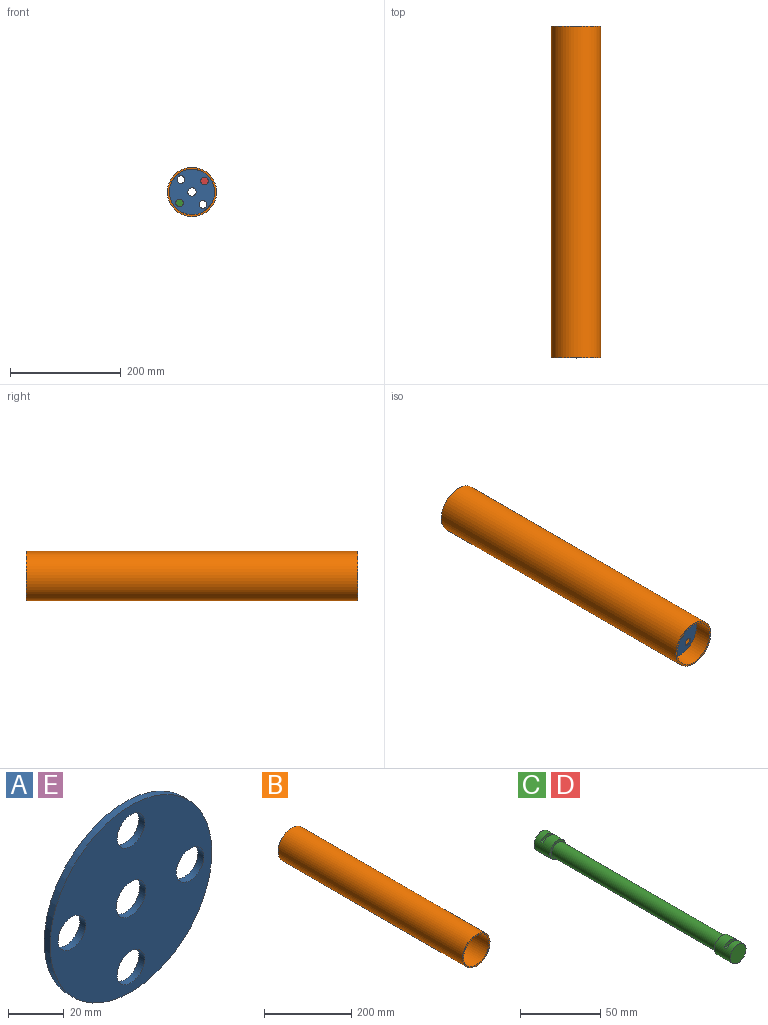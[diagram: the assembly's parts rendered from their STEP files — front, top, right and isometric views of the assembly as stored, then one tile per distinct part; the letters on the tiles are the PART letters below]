
ASSEMBLY  parts=5 mates=8
PART A: 8 faces, bbox 82x3x82 mm
  f0: cylinder r=7mm len=14mm, axis (0,1,0), area 131.9mm2, adj f5,f6
  f1: cylinder r=7mm len=14mm, axis (0,1,0), area 131.9mm2, adj f5,f6
  f2: cylinder r=7mm len=14mm, axis (0,1,0), area 131.9mm2, adj f5,f6
  f3: cylinder r=7mm len=14mm, axis (0,1,0), area 131.9mm2, adj f5,f6
  f4: cylinder r=41mm len=82mm, axis (0,1,0), area 772.8mm2, adj f5,f6
  f5: plane 82x82mm, normal (0,-1,0), area 4488.6mm2, adj f0,f1,f2,f3,f4,f7
  f6: plane 82x82mm, normal (0,1,0), area 4488.6mm2, adj f0,f1,f2,f3,f4,f7
  f7: cylinder r=7.5mm len=15mm, axis (0,-1,0), area 141.4mm2, adj f5,f6
PART B: 4 faces, bbox 89x600x89 mm
  f0: cylinder r=41.2mm len=600mm, axis (0,1,0), area 155320.3mm2, adj f2,f3
  f1: cylinder r=44.5mm len=600mm, axis (0,1,0), area 167761mm2, adj f2,f3
  f2: plane 89x89mm, normal (0,-1,0), area 888.5mm2, adj f0,f1
  f3: plane 89x89mm, normal (0,1,0), area 888.5mm2, adj f0,f1
PART C: 19 faces, bbox 14x173x14 mm
  f0: cylinder r=7mm len=14mm, axis (0,1,0), area 556mm2, adj f3,f4,f13,f14,f15,f16,f17,f18
  f1: cylinder r=7mm len=14mm, axis (0,-1,0), area 556mm2, adj f5,f6,f7,f8,f9,f10,f11,f12
  f2: cylinder r=5.5mm len=145mm, axis (0,1,0), area 5010.8mm2, adj f4,f6
  f3: plane 14x14mm, normal (0,-1,0), area 153.9mm2, adj f0
  f4: plane 14x14mm, normal (0,1,0), area 58.9mm2, adj f0,f2
  f5: plane 14x14mm, normal (0,1,0), area 153.9mm2, adj f1
  f6: plane 14x14mm, normal (0,-1,0), area 58.9mm2, adj f1,f2
  f7: plane 11.2x2.8mm, normal (0,1,0), area 21.9mm2, adj f1,f8
  f8: plane 11.2x2.3mm, normal (0,0,1), area 25.8mm2, adj f1,f7,f9
  f9: plane 11.2x2.8mm, normal (0,-1,0), area 21.9mm2, adj f1,f8
  f10: plane 11.2x2.8mm, normal (0,-1,0), area 21.9mm2, adj f1,f11
  f11: plane 11.2x2.3mm, normal (0,0,-1), area 25.8mm2, adj f1,f10,f12
  f12: plane 11.2x2.8mm, normal (0,1,0), area 21.9mm2, adj f1,f11
  f13: plane 11.2x2.8mm, normal (0,-1,0), area 21.9mm2, adj f0,f14
  f14: plane 11.2x2.3mm, normal (0,0,-1), area 25.8mm2, adj f0,f13,f15
  f15: plane 11.2x2.8mm, normal (0,1,0), area 21.9mm2, adj f0,f14
  f16: plane 11.2x2.3mm, normal (0,0,1), area 25.8mm2, adj f0,f17,f18
  f17: plane 11.2x2.8mm, normal (0,-1,0), area 21.9mm2, adj f0,f16
  f18: plane 11.2x2.8mm, normal (0,1,0), area 21.9mm2, adj f0,f16
PART D: same geometry as C
PART E: same geometry as A
PLACE A rot(axis=(0,1,0),138.5deg) t=(-209.89,34.2,19.51)mm
PLACE B t=(-209.89,597.89,19.51)mm fixed
PLACE C t=(-232.37,190.2,-0.36)mm
PLACE D rot(axis=(0,-1,0),77deg) t=(-187.41,190.2,39.37)mm
PLACE E rot(axis=(0,1,0),138.5deg) t=(-209.89,204.2,19.51)mm
MATE planar D.f0 <-> C.f0  axis (0,-1,0) through (-187.41,31.2,39.37)mm
MATE cylindrical A.f0 <-> C.f0  axis (0,-1,0) through (-232.37,31.2,-0.36)mm
MATE cylindrical E.f0 <-> C.f1  axis (0,1,0) through (-232.37,204.2,-0.36)mm
MATE cylindrical D.f1 <-> E.f2  axis (0,-1,0) through (-187.41,197.2,39.37)mm
MATE cylindrical D.f0 <-> A.f2  axis (0,1,0) through (-187.41,45.2,39.37)mm
MATE cylindrical B.f0 <-> A.f7  axis (0,1,0) through (-209.89,-2.11,19.51)mm
MATE planar A.f7 <-> C.f0  axis (0,-1,0) through (-209.89,31.2,19.51)mm
MATE planar E.f4 <-> C.f1  axis (0,1,0) through (-209.89,204.2,19.51)mm
